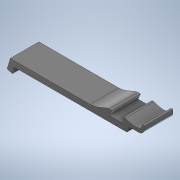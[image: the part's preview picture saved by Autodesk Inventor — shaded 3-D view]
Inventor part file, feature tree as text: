
AUTODESK INVENTOR PART (.ipt)
format: ipt  version: 2020 (Build 240168000, 168)  size: 221,184 bytes
history: native  units: mm
features: extrude x4, sketch x3, projected_geometry x2, other x1
ambient origin geometry x8: Origin, YZ Plane, XZ Plane, XY Plane, X Axis, Y Axis, Z Axis, Center Point
bodies: Body1 (feature_tree)
feature tree (10):
  other  "Твердое тело1"
  extrude  "Выдавливание1"  Depth=9.0mm
  extrude  "Выдавливание2"  Depth=3.0mm
  sketch  "Эскиз4"
  extrude  "Выдавливание3"  Depth=3.0mm
  extrude  "Выдавливание4"  Depth=2.5mm
  sketch  "Эскиз1"
  sketch  "Эскиз3"
  projected_geometry  "Спроецированная петля1"
  projected_geometry  "Спроецированная петля2"
